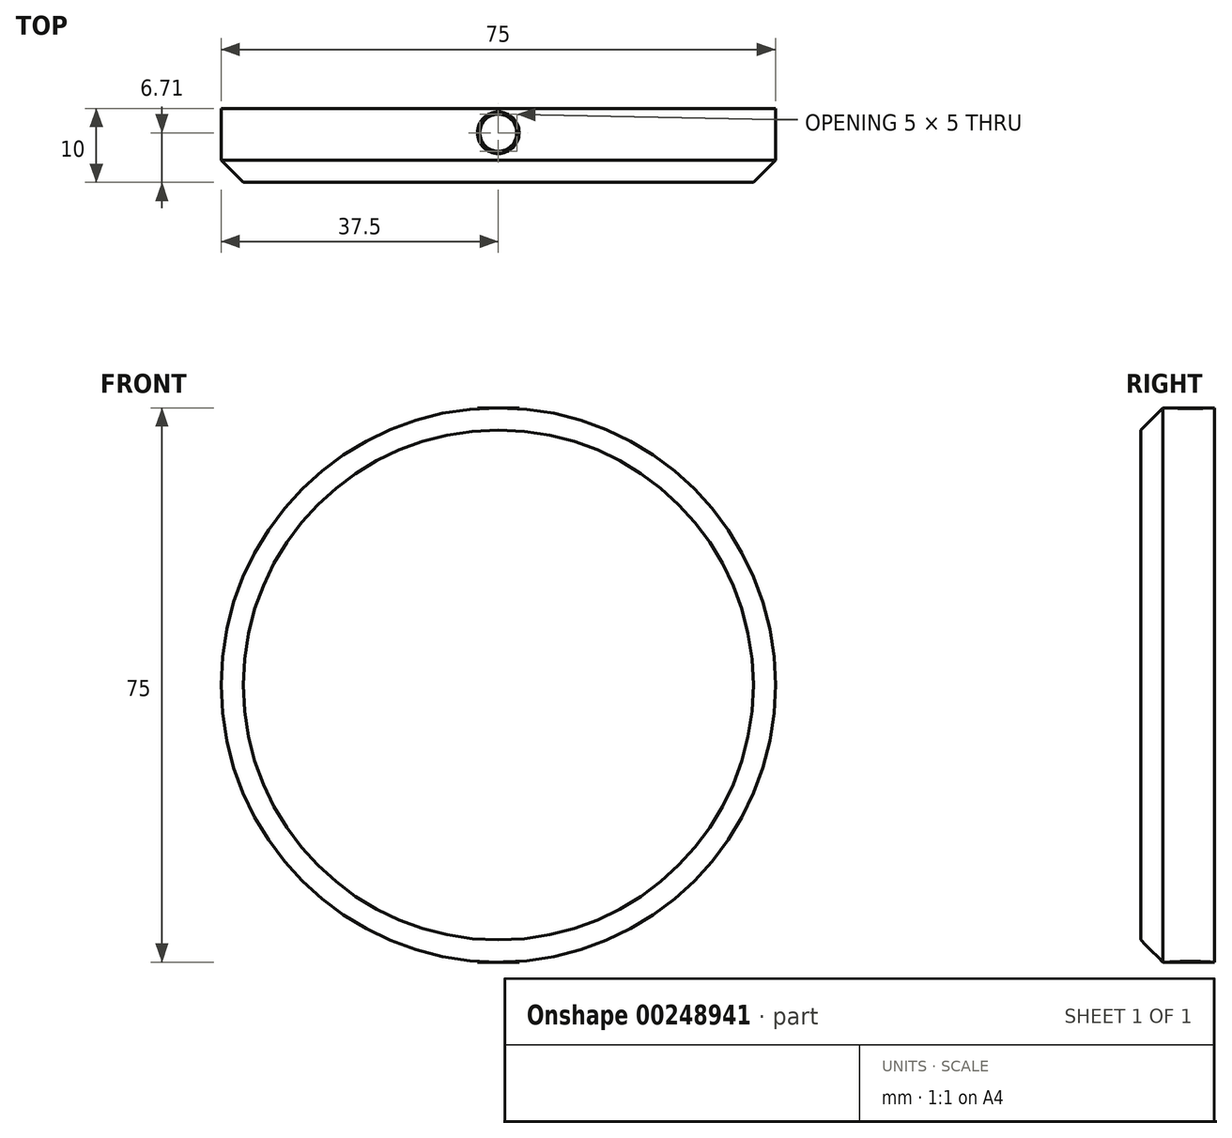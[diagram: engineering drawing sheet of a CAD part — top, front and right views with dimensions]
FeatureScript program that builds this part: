
annotation { "Feature Type Name" : "Feature", "Feature Type Description" : "" }
export const myFeature = defineFeature(function(context is Context, id is Id, definition is map)
    precondition{}
    {
        {
            var Q0;
            Q0=qCreatedBy(makeId("Front.planeOp"),FACE);
            var sketch = newSketch(context, id + "F0", { "sketchPlane" : qUnion([Q0])});
            skPoint(sketch, "E0.orphan", {"position": v(0, -129.07) * mm});
            skLineSegment(sketch, "E1", {"start": v(0, 88.91) * mm, "end": v(0, -176.19) * mm});
            skCircle(sketch, "E2", {"center": v(0, 0) * mm, "radius": 37.5 * mm});
            skSolve(sketch);
        }
        {
            var Q0;
            {var subQ0=sQuery(id+"F0.wireOp",EDGE,"E2");var subQ1=sQuery(id+"F0.wireOp",EDGE,"E1");var subQ2=makeQuery(id+"F0.imprint","INTERSECT",VERTEX,{"disambiguationData":[OD(0.0)],"derivedFrom":[subQ1,subQ0]});Q0=makeQuery(id+"F0.imprint","IMPRINT",FACE,{"disambiguationData":[TD([[makeQuery(id+"F0.imprint","IMPRINT",EDGE,{"disambiguationData":[TD([[subQ2,1.0]])],"derivedFrom":subQ1}),-1.0]])]});}
            var Q1;
            {var subQ0=sQuery(id+"F0.wireOp",EDGE,"E2");var subQ1=sQuery(id+"F0.wireOp",EDGE,"E1");var subQ2=makeQuery(id+"F0.imprint","INTERSECT",VERTEX,{"disambiguationData":[OD(0.0)],"derivedFrom":[subQ1,subQ0]});Q1=makeQuery(id+"F0.imprint","IMPRINT",FACE,{"disambiguationData":[TD([[makeQuery(id+"F0.imprint","IMPRINT",EDGE,{"disambiguationData":[TD([[subQ2,1.0]])],"derivedFrom":subQ1}),1.0]])]});}
            var Q2;
            Q2=sQuery(id+"F0.wireOp",EDGE,"E2");
            extrude(context, id + "F1", {"entities" : qUnion([Q0, Q1]), "surfaceEntities" : qUnion([Q2]), "depth" : 10 * mm});
        }
        {
            var Q0;
            Q0=makeQuery(id+"F1.opExtrude","CAP_EDGE",EDGE,{"disambiguationData":[OSD([sQuery(id+"F0.wireOp",EDGE,"E2")])],"isStart":false});
            chamfer(context, id + "F2", {"entities" : qUnion([Q0]), "width" : 3 * mm});
        }
        {
            var Q0;
            Q0=qCreatedBy(makeId("Top.planeOp"),FACE);
            var sketch = newSketch(context, id + "F3", { "sketchPlane" : qUnion([Q0])});
            skCircle(sketch, "E3", {"center": v(0, -3.3) * mm, "radius": 2.5 * mm});
            skCircle(sketch, "E4", {"center": v(0, -3.3) * mm, "radius": 2.82 * mm});
            skSolve(sketch);
        }
        {
            var Q0;
            Q0=qSketchRegion(id+"F3",true);
            extrude(context, id + "F4", {"entities" : qUnion([Q0]), "operationType" : NewBodyOperationType.ADD, "endBound" : BoundingType.SYMMETRIC, "depth" : 75 * mm});
        }
        {
            var Q0;
            Q0=makeQuery(id+"F4.opExtrude","CAP_FACE",FACE,{"disambiguationData":[OSD([sQuery(id+"F3.wireOp",EDGE,"E3"),sQuery(id+"F3.wireOp",EDGE,"E4")])],"isStart":true});
            extrude(context, id + "F5", {"entities" : qUnion([Q0]), "operationType" : NewBodyOperationType.ADD, "oppositeDirection" : true, "depth" : 75 * mm});
        }
    });
